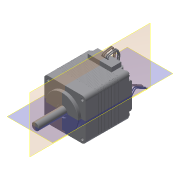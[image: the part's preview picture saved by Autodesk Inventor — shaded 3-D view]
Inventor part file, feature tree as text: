
AUTODESK INVENTOR PART (.ipt)
format: ipt  version: 2022 (Build 260153000, 153)  size: 3,344,896 bytes
history: native  units: mm
features: other x8, plane x2
ambient origin geometry x8: Origin, YZ Plane, XZ Plane, XY Plane, X Axis, Y Axis, Z Axis, Center Point
bodies: Solid1 (feature_tree), Solid2 (feature_tree), Solid3 (feature_tree), Solid4 (feature_tree), Solid5 (feature_tree), Solid6 (feature_tree), Solid7 (feature_tree), Solid8 (feature_tree)
feature tree (10):
  plane  "Work Plane1"
  plane  "Arbeitsebene2"
  other  "Lagerschild_11_1:1"
  other  "Welle_11_2:1"
  other  "Kollektorschild_11_3:1"
  other  "Schraube_M2x25_4:1"
  other  "Schraube_M2x25_5:1"
  other  "Schraube_M2x25_6:1"
  other  "Schraube_M2x25_7:1"
  other  "Stator_11_8:1"
